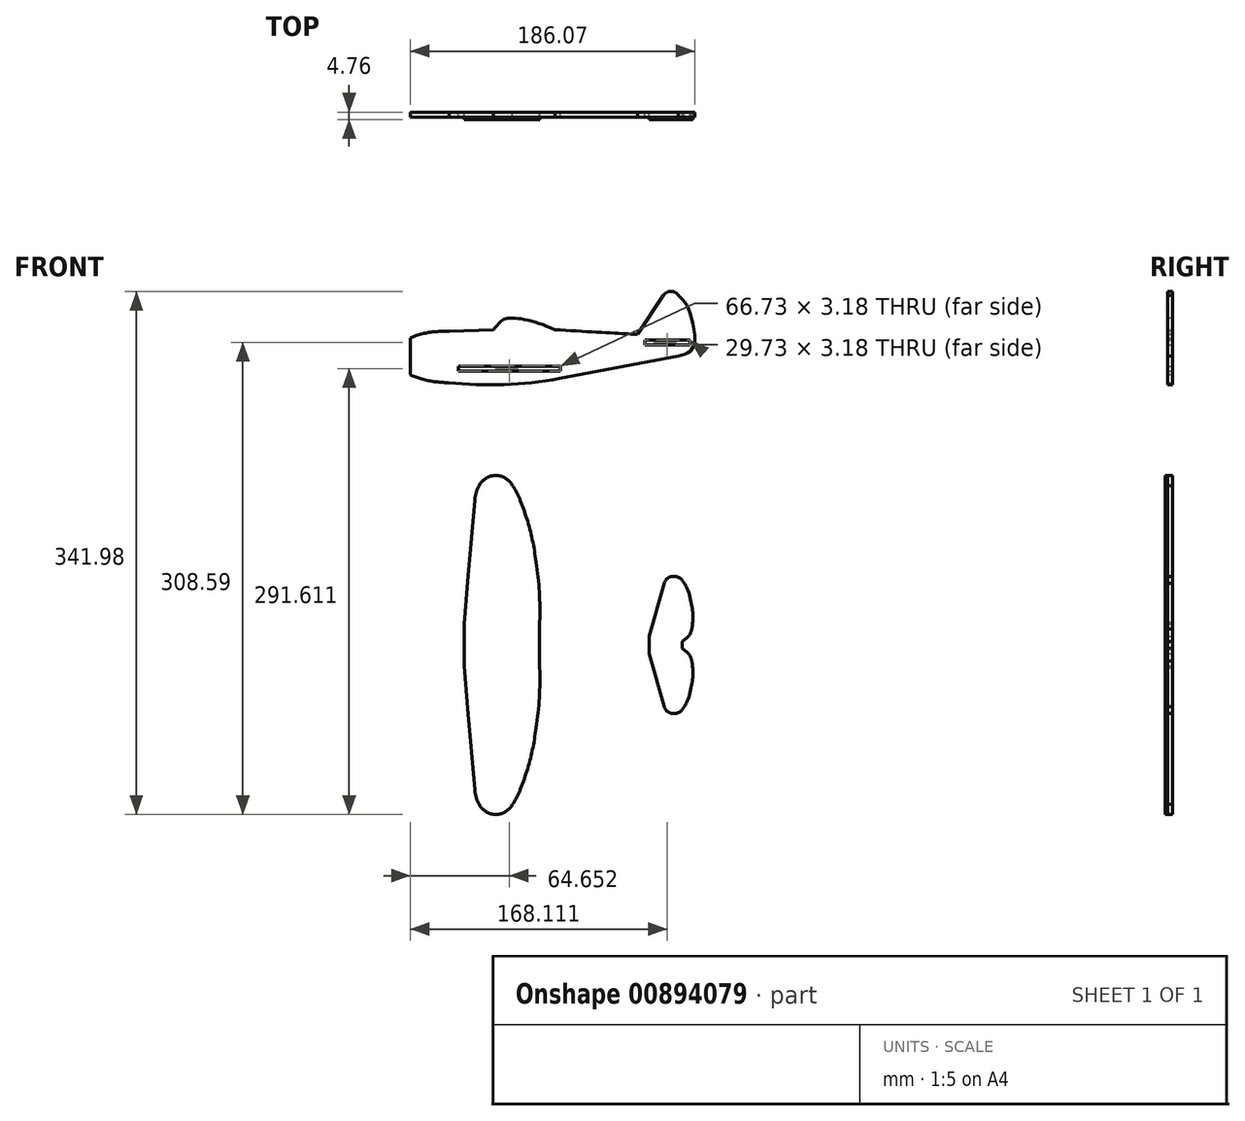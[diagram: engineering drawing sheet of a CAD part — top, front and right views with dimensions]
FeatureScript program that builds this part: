
annotation { "Feature Type Name" : "Feature", "Feature Type Description" : "" }
export const myFeature = defineFeature(function(context is Context, id is Id, definition is map)
    precondition{}
    {
        {
            var Q0;
            Q0=qCreatedBy(makeId("Front.planeOp"),FACE);
            var sketch = newSketch(context, id + "F0", { "sketchPlane" : qUnion([Q0])});
            skLineSegment(sketch, "E0", {"start": v(-218.06, 115.34) * mm, "end": v(-30.27, 115.34) * mm, "construction": true});
            skLineSegment(sketch, "E1", {"start": v(-181.95, 129.04) * mm, "end": v(-181.95, 115.34) * mm});
            skLineSegment(sketch, "E2", {"start": v(-181.95, 129.04) * mm, "end": v(-179.45, 160.87) * mm});
            skLineSegment(sketch, "E3", {"start": v(-179.45, 160.87) * mm, "end": v(-175.17, 210.07) * mm});
            skArc(sketch, "E4", {"start": v(-175.17, 210.07) * mm, "mid": v(-174.24, 214.98) * mm, "end": v(-172.34, 219.6) * mm});
            skArc(sketch, "E5", {"start": v(-172.34, 219.6) * mm, "mid": v(-161.4, 226.15) * mm, "end": v(-150.48, 219.6) * mm});
            skLineSegment(sketch, "E6", {"start": v(-145.38, 210.07) * mm, "end": v(-142.82, 202.94) * mm});
            skArc(sketch, "E7", {"start": v(-145.38, 210.07) * mm, "mid": v(-147.58, 215.02) * mm, "end": v(-150.48, 219.6) * mm});
            skArc(sketch, "E8", {"start": v(-142.82, 202.94) * mm, "mid": v(-138.66, 189.28) * mm, "end": v(-135.85, 175.27) * mm});
            skLineSegment(sketch, "E9", {"start": v(-135.85, 175.27) * mm, "end": v(-134.97, 169.44) * mm});
            skArc(sketch, "E10", {"start": v(-134.97, 169.44) * mm, "mid": v(-132.94, 149.87) * mm, "end": v(-132.68, 130.2) * mm});
            skLineSegment(sketch, "E11", {"start": v(-132.68, 130.2) * mm, "end": v(-132.68, 115.34) * mm});
            skPoint(sketch, "E11.endSnap0", {"position": v(-124.17, 115.34) * mm});
            skLineSegment(sketch, "E12", {"start": v(-61.14, 115.34) * mm, "end": v(-61.14, 121.04) * mm});
            skLineSegment(sketch, "E13", {"start": v(-61.14, 121.04) * mm, "end": v(-51.25, 155.7) * mm});
            skArc(sketch, "E14", {"start": v(-51.25, 155.7) * mm, "mid": v(-49.12, 158.88) * mm, "end": v(-45.53, 160.21) * mm});
            skArc(sketch, "E15", {"start": v(-45.53, 160.21) * mm, "mid": v(-41.15, 159.08) * mm, "end": v(-38.13, 155.7) * mm});
            skFitSpline(sketch, "E16", {"points": [v(-38.13, 155.7) * mm, v(-36.84, 153.45) * mm, v(-34.83, 148.38) * mm, v(-33.3, 141.54) * mm, v(-32.5, 136.15) * mm, v(-32.57, 130.6) * mm, v(-33.22, 125.85) * mm, v(-33.3, 125.85) * mm, v(-33.54, 126) * mm], "startDerivative": vector(11.08, -17.97) * mm, "endDerivative": vector(-7.2, 5.03) * mm});
            skFitSpline(sketch, "E17", {"points": [v(-33.22, 125.85) * mm, v(-34.26, 122.63) * mm, v(-36.52, 119.9) * mm, v(-38.27, 118.45) * mm, v(-39.62, 117.44) * mm], "startDerivative": vector(-2.62, -11.7) * mm, "endDerivative": vector(-6.64, -4.95) * mm});
            skLineSegment(sketch, "E18", {"start": v(-39.62, 117.44) * mm, "end": v(-39.62, 115.34) * mm});
            skLineSegment(sketch, "E19", {"start": v(-217.28, 316.11) * mm, "end": v(-217.28, 292.07) * mm});
            skFitSpline(sketch, "E20", {"points": [v(-217.28, 292.07) * mm, v(-192.3, 286.88) * mm], "startDerivative": vector(16.86, -9.6) * mm, "endDerivative": vector(26.06, 0) * mm});
            skFitSpline(sketch, "E21", {"points": [v(-191.94, 320.45) * mm, v(-163, 321.5) * mm], "startDerivative": vector(28.93, 1.06) * mm, "endDerivative": vector(28.93, 1.06) * mm});
            skFitSpline(sketch, "E22", {"points": [v(-163, 321.5) * mm, v(-154.08, 328.85) * mm, v(-122.8, 321.5) * mm], "startDerivative": vector(32.76, 37.05) * mm, "endDerivative": vector(58.97, -28) * mm});
            skFitSpline(sketch, "E23", {"points": [v(-122.8, 321.5) * mm, v(-68.92, 318.4) * mm, v(-68.68, 318.4) * mm], "startDerivative": vector(82.62, -4.86) * mm, "endDerivative": vector(2.2, 0.1) * mm});
            skFitSpline(sketch, "E24", {"points": [v(-68.68, 318.4) * mm, v(-51.8, 343.85) * mm], "startDerivative": vector(16.88, 25.44) * mm, "endDerivative": vector(16.88, 25.44) * mm});
            skArc(sketch, "E25", {"start": v(-51.8, 343.85) * mm, "mid": v(-46.83, 346.51) * mm, "end": v(-41.87, 343.85) * mm});
            skFitSpline(sketch, "E26", {"points": [v(-41.87, 343.85) * mm, v(-36.4, 337.15) * mm, v(-32.68, 326.47) * mm, v(-31.44, 319.27) * mm, v(-31.44, 312.94) * mm, v(-34.3, 307.48) * mm, v(-41.87, 304.13) * mm], "startDerivative": vector(33.83, -34.05) * mm, "endDerivative": vector(-50.21, -15.08) * mm});
            skLineSegment(sketch, "E27", {"start": v(-41.87, 304.13) * mm, "end": v(-119.81, 289.6) * mm});
            skArc(sketch, "E28", {"start": v(-119.81, 289.6) * mm, "mid": v(-155.95, 285.58) * mm, "end": v(-192.3, 286.88) * mm});
            skFitSpline(sketch, "E29", {"points": [v(-217.28, 316.11) * mm, v(-191.94, 320.45) * mm], "startDerivative": vector(27.02, 11.86) * mm, "endDerivative": vector(26.34, -0.23) * mm});
            skLineSegment(sketch, "E30.MirrorCS", {"start": v(-181.95, 101.64) * mm, "end": v(-181.95, 115.34) * mm});
            skLineSegment(sketch, "E31.MirrorCS", {"start": v(-181.95, 101.64) * mm, "end": v(-179.45, 69.8) * mm});
            skLineSegment(sketch, "E32.MirrorCS", {"start": v(-179.45, 69.8) * mm, "end": v(-175.17, 20.6) * mm});
            skArc(sketch, "E33.MirrorCS", {"start": v(-172.34, 11.09) * mm, "mid": v(-161.4, 4.53) * mm, "end": v(-150.48, 11.09) * mm});
            skArc(sketch, "E34.MirrorCS", {"start": v(-145.38, 20.6) * mm, "mid": v(-147.58, 15.66) * mm, "end": v(-150.48, 11.09) * mm});
            skLineSegment(sketch, "E35.MirrorCS", {"start": v(-145.38, 20.6) * mm, "end": v(-142.82, 27.74) * mm});
            skArc(sketch, "E36.MirrorCS", {"start": v(-142.82, 27.74) * mm, "mid": v(-138.66, 41.4) * mm, "end": v(-135.85, 55.4) * mm});
            skLineSegment(sketch, "E37.MirrorCS", {"start": v(-135.85, 55.4) * mm, "end": v(-134.97, 61.24) * mm});
            skArc(sketch, "E38.MirrorCS", {"start": v(-134.97, 61.24) * mm, "mid": v(-132.94, 80.8) * mm, "end": v(-132.68, 100.48) * mm});
            skLineSegment(sketch, "E39.MirrorCS", {"start": v(-132.68, 100.48) * mm, "end": v(-132.68, 115.34) * mm});
            skArc(sketch, "E40.MirrorCS", {"start": v(-175.17, 20.6) * mm, "mid": v(-174.24, 15.7) * mm, "end": v(-172.34, 11.09) * mm});
            skLineSegment(sketch, "E41.MirrorCS", {"start": v(-61.14, 115.34) * mm, "end": v(-61.14, 109.64) * mm});
            skLineSegment(sketch, "E42.MirrorCS", {"start": v(-61.14, 109.64) * mm, "end": v(-51.25, 74.97) * mm});
            skArc(sketch, "E43.MirrorCS", {"start": v(-51.25, 74.97) * mm, "mid": v(-49.12, 71.8) * mm, "end": v(-45.53, 70.46) * mm});
            skArc(sketch, "E44.MirrorCS", {"start": v(-45.53, 70.46) * mm, "mid": v(-41.15, 71.6) * mm, "end": v(-38.13, 74.97) * mm});
            skFitSpline(sketch, "E45.MirrorCS", {"points": [v(-38.13, 74.97) * mm, v(-36.84, 77.23) * mm, v(-34.83, 82.3) * mm, v(-33.3, 89.14) * mm, v(-32.5, 94.53) * mm, v(-32.57, 100.08) * mm, v(-33.22, 104.83) * mm, v(-33.3, 104.83) * mm, v(-33.54, 104.67) * mm], "startDerivative": vector(11.08, 17.97) * mm, "endDerivative": vector(-7.2, -5.03) * mm});
            skFitSpline(sketch, "E46.MirrorCS", {"points": [v(-33.22, 104.83) * mm, v(-34.26, 108.05) * mm, v(-36.52, 110.79) * mm, v(-38.27, 112.23) * mm, v(-39.62, 113.24) * mm], "startDerivative": vector(-2.62, 11.7) * mm, "endDerivative": vector(-6.64, 4.95) * mm});
            skLineSegment(sketch, "E47.MirrorCS", {"start": v(-39.62, 113.24) * mm, "end": v(-39.62, 115.34) * mm});
            skSolve(sketch);
        }
        {
            var Q0;
            Q0=makeQuery(id+"F0.imprint","IMPRINT",FACE,{"disambiguationData":[TD([[makeQuery(id+"F0.imprint","IMPRINT",EDGE,{"derivedFrom":sQuery(id+"F0.wireOp",EDGE,"E19")}),1.0]])]});
            var Q1;
            Q1=makeQuery(id+"F0.imprint","IMPRINT",FACE,{"disambiguationData":[TD([[makeQuery(id+"F0.imprint","IMPRINT",EDGE,{"derivedFrom":sQuery(id+"F0.wireOp",EDGE,"E1")}),1.0]])]});
            var Q2;
            Q2=makeQuery(id+"F0.imprint","IMPRINT",FACE,{"disambiguationData":[TD([[makeQuery(id+"F0.imprint","IMPRINT",EDGE,{"derivedFrom":sQuery(id+"F0.wireOp",EDGE,"E12")}),-1.0]])]});
            var Q3;
            Q3 = qSketchRegion(id + "F2", true);
            extrude(context, id + "F1", {"entities" : qUnion([Q0, Q1, Q2, Q3]), "depth" : 3.17 * mm, "offsetDistance" : 25.4 * mm});
        }
        {
            var Q0;
            Q0=qCreatedBy(makeId("Front.planeOp"),FACE);
            var sketch = newSketch(context, id + "F2", { "sketchPlane" : qUnion([Q0])});
            skLineSegment(sketch, "E48.bottom", {"start": v(-186, 297.73) * mm, "end": v(-119.26, 297.73) * mm});
            skLineSegment(sketch, "E48.top", {"start": v(-186, 294.55) * mm, "end": v(-119.26, 294.55) * mm});
            skLineSegment(sketch, "E48.left", {"start": v(-186, 297.73) * mm, "end": v(-186, 294.55) * mm});
            skLineSegment(sketch, "E48.right", {"start": v(-119.26, 297.73) * mm, "end": v(-119.26, 294.55) * mm});
            skLineSegment(sketch, "E49.bottom", {"start": v(-64.04, 314.7) * mm, "end": v(-34.3, 314.7) * mm});
            skLineSegment(sketch, "E49.top", {"start": v(-64.04, 311.53) * mm, "end": v(-34.3, 311.53) * mm});
            skLineSegment(sketch, "E49.left", {"start": v(-34.3, 314.7) * mm, "end": v(-34.3, 311.53) * mm});
            skLineSegment(sketch, "E49.right", {"start": v(-64.04, 314.7) * mm, "end": v(-64.04, 311.53) * mm});
            skSolve(sketch);
        }
        {
            var Q0;
            Q0 = qSketchRegion(id + "F2", true);
            extrude(context, id + "F3", {"entities" : qUnion([Q0]), "operationType" : NewBodyOperationType.REMOVE, "endBound" : BoundingType.THROUGH_ALL, "depth" : 25.4 * mm, "offsetDistance" : 25.4 * mm});
        }
        {
            var Q0;
            Q0=makeQuery(id+"F1.opExtrude","CAP_FACE",FACE,{"disambiguationData":[OSD([sQuery(id+"F0.wireOp",EDGE,"E1"),sQuery(id+"F0.wireOp",EDGE,"E2"),sQuery(id+"F0.wireOp",EDGE,"E3"),sQuery(id+"F0.wireOp",EDGE,"E4"),sQuery(id+"F0.wireOp",EDGE,"E5"),sQuery(id+"F0.wireOp",EDGE,"E6"),sQuery(id+"F0.wireOp",EDGE,"E7"),sQuery(id+"F0.wireOp",EDGE,"E8"),sQuery(id+"F0.wireOp",EDGE,"E9"),sQuery(id+"F0.wireOp",EDGE,"E10"),sQuery(id+"F0.wireOp",EDGE,"E11"),sQuery(id+"F0.wireOp",EDGE,"E30.MirrorCS"),sQuery(id+"F0.wireOp",EDGE,"E31.MirrorCS"),sQuery(id+"F0.wireOp",EDGE,"E32.MirrorCS"),sQuery(id+"F0.wireOp",EDGE,"E33.MirrorCS"),sQuery(id+"F0.wireOp",EDGE,"E34.MirrorCS"),sQuery(id+"F0.wireOp",EDGE,"E35.MirrorCS"),sQuery(id+"F0.wireOp",EDGE,"E36.MirrorCS"),sQuery(id+"F0.wireOp",EDGE,"E37.MirrorCS"),sQuery(id+"F0.wireOp",EDGE,"E38.MirrorCS"),sQuery(id+"F0.wireOp",EDGE,"E39.MirrorCS"),sQuery(id+"F0.wireOp",EDGE,"E40.MirrorCS")])],"isStart":false});
            var Q1;
            Q1=makeQuery(id+"F1.opExtrude","CAP_FACE",FACE,{"disambiguationData":[OSD([sQuery(id+"F0.wireOp",EDGE,"E12"),sQuery(id+"F0.wireOp",EDGE,"E13"),sQuery(id+"F0.wireOp",EDGE,"E14"),sQuery(id+"F0.wireOp",EDGE,"E15"),sQuery(id+"F0.wireOp",EDGE,"E16"),sQuery(id+"F0.wireOp",EDGE,"E17"),sQuery(id+"F0.wireOp",EDGE,"E18"),sQuery(id+"F0.wireOp",EDGE,"E41.MirrorCS"),sQuery(id+"F0.wireOp",EDGE,"E42.MirrorCS"),sQuery(id+"F0.wireOp",EDGE,"E43.MirrorCS"),sQuery(id+"F0.wireOp",EDGE,"E44.MirrorCS"),sQuery(id+"F0.wireOp",EDGE,"E45.MirrorCS"),sQuery(id+"F0.wireOp",EDGE,"E46.MirrorCS"),sQuery(id+"F0.wireOp",EDGE,"E47.MirrorCS")])],"isStart":false});
            extrude(context, id + "F4", {"entities" : qUnion([Q0, Q1]), "depth" : 1.59 * mm, "offsetDistance" : 25.4 * mm});
        }
    });
